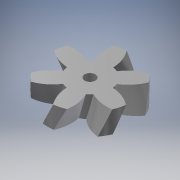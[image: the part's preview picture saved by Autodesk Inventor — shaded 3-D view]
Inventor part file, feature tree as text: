
AUTODESK INVENTOR PART (.ipt)
format: ipt  version: 2017 SP1 (Build 210196100, 196)  size: 462,336 bytes
history: native  units: mm (DEFAULTED — no unit token found)
features: plane x3, other x3, sketch x3, extrude x2
ambient origin geometry x8: Origin, YZ Plane, XZ Plane, XY Plane, X Axis, Y Axis, Z Axis, Center Point
bodies: Solid1 (feature_tree)
feature tree (11):
  extrude  "Extrusion1"  Depth=10.0mm TaperAngle=0.0deg
  plane  "Work Plane2"
  plane  "Work Plane8"
  plane  "Work Plane9"
  other  "Engrenage cylindrique"
  extrude  "Extrusion2"  Depth=10.0mm TaperAngle=0.0deg
  sketch  "Sketch1"  dims[d0=38.885336mm d1=10.0mm d2=0.0mm]
  sketch  "Sketch2"  dims[d3=30.066593mm d4=10.0mm d5=0.0mm d16=30.066593mm d17=0.0mm d34=30.0deg d39=0.0mm d41=0.0mm d43=30.066593mm d46=30.066593mm d47=0.0mm d48=0.0mm d49=5.0mm d50=10.0mm d51=0.0mm]
  other  "Srf1"
  sketch  "Esquisse3"
  other  "Diamètre primitif"
